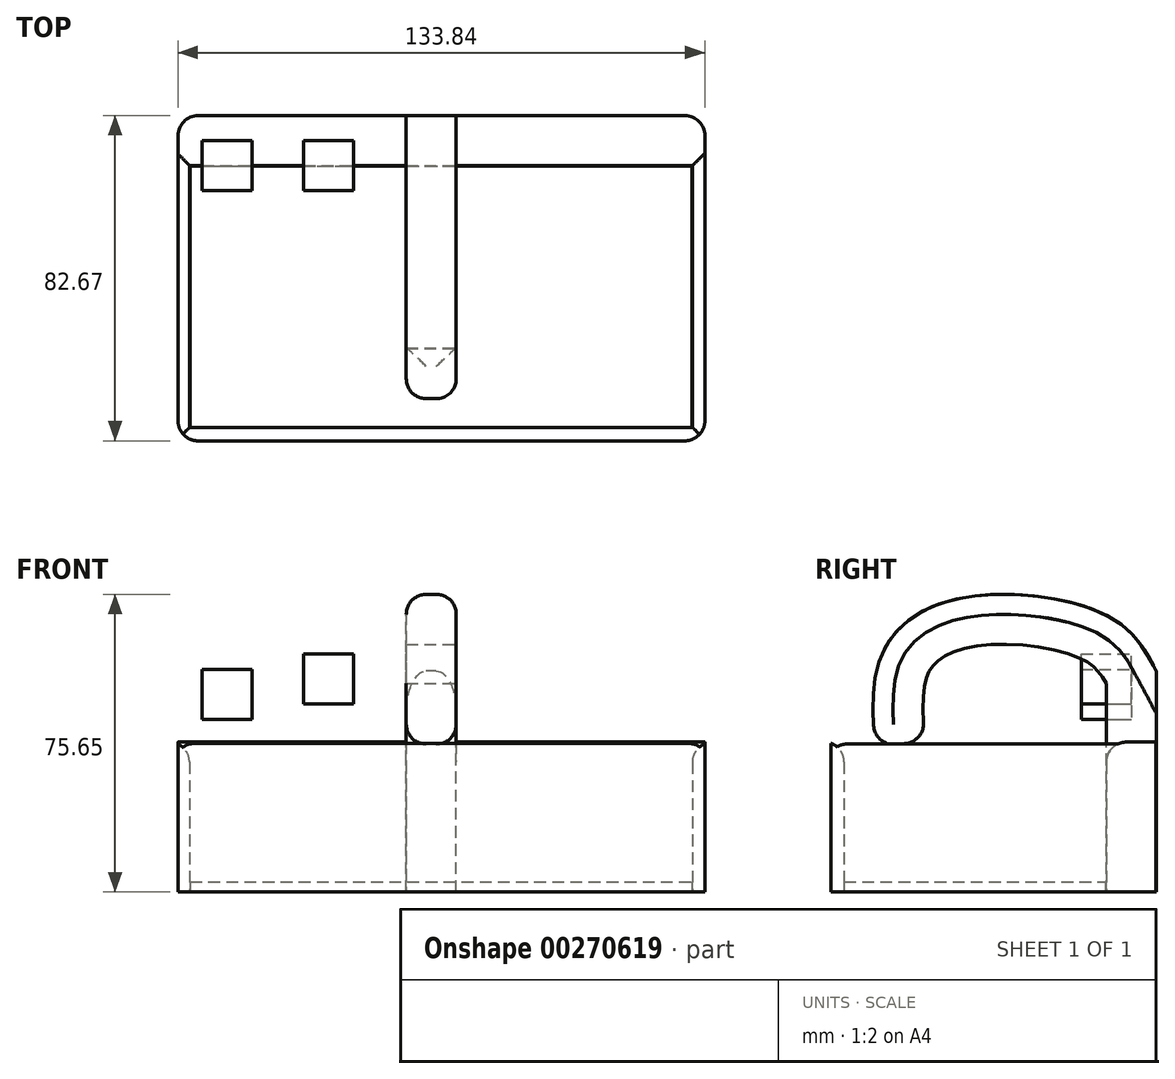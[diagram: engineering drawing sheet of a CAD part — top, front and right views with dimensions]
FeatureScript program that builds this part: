
annotation { "Feature Type Name" : "Feature", "Feature Type Description" : "" }
export const myFeature = defineFeature(function(context is Context, id is Id, definition is map)
    precondition{}
    {
        {
            var Q0;
            Q0=qCreatedBy(makeId("Top.planeOp"),FACE);
            var sketch = newSketch(context, id + "F0", { "sketchPlane" : qUnion([Q0])});
            skLineSegment(sketch, "E0.bottom", {"start": v(-6.35, 6.35) * mm, "end": v(6.35, 6.35) * mm});
            skLineSegment(sketch, "E0.top", {"start": v(-6.35, -6.35) * mm, "end": v(6.35, -6.35) * mm});
            skLineSegment(sketch, "E0.left", {"start": v(-6.35, 6.35) * mm, "end": v(-6.35, -6.35) * mm});
            skLineSegment(sketch, "E0.right", {"start": v(6.35, 6.35) * mm, "end": v(6.35, -6.35) * mm});
            skPoint(sketch, "E0.middle", {"position": v(0, 0) * mm});
            skSolve(sketch);
        }
        {
            var Q0;
            Q0=qCreatedBy(makeId("Right.planeOp"),FACE);
            var sketch = newSketch(context, id + "F1", { "sketchPlane" : qUnion([Q0])});
            skLineSegment(sketch, "E1", {"start": v(0, 0) * mm, "end": v(0, 54.57) * mm});
            skLineSegment(sketch, "E2", {"start": v(0, -0.8) * mm, "end": v(0, -38.9) * mm});
            skFitSpline(sketch, "E3", {"points": [v(0, 54.57) * mm, v(-8.3, 64.16) * mm, v(-40.1, 68.78) * mm, v(-57.07, 58.87) * mm, v(-58.75, 37.62) * mm], "startDerivative": vector(-28.75, 53.69) * mm, "endDerivative": vector(7.18, -92.92) * mm});
            skSolve(sketch);
        }
        {
            var Q0;
            Q0=makeQuery(id+"F0.imprint","IMPRINT",FACE,{"disambiguationData":[TD([[makeQuery(id+"F0.imprint","IMPRINT",EDGE,{"derivedFrom":sQuery(id+"F0.wireOp",EDGE,"E0.bottom")}),-1.0]])]});
            var Q1;
            Q1=sQuery(id+"F1.wireOp",EDGE,"E3");
            var Q2;
            Q2=sQuery(id+"F1.wireOp",EDGE,"E1");
            sweep(context, id + "F2", {"profiles" : qUnion([Q0]), "path" : qUnion([Q1, Q2])});
        }
        {
            var Q0;
            Q0=qCreatedBy(makeId("Top.planeOp"),FACE);
            var sketch = newSketch(context, id + "F3", { "sketchPlane" : qUnion([Q0])});
            skLineSegment(sketch, "E4.bottom", {"start": v(-64.34, 6.27) * mm, "end": v(69.5, 6.27) * mm});
            skLineSegment(sketch, "E4.top", {"start": v(-64.34, -76.32) * mm, "end": v(69.5, -76.32) * mm});
            skLineSegment(sketch, "E4.left", {"start": v(-64.34, 6.27) * mm, "end": v(-64.34, -76.32) * mm});
            skLineSegment(sketch, "E4.right", {"start": v(69.5, 6.27) * mm, "end": v(69.5, -76.32) * mm});
            skLineSegment(sketch, "E5.bottom", {"start": v(-61.44, -6.33) * mm, "end": v(66.42, -6.33) * mm});
            skLineSegment(sketch, "E5.top", {"start": v(-61.44, -72.94) * mm, "end": v(66.42, -72.94) * mm});
            skLineSegment(sketch, "E5.left", {"start": v(-61.44, -6.33) * mm, "end": v(-61.44, -72.94) * mm});
            skLineSegment(sketch, "E5.right", {"start": v(66.42, -6.33) * mm, "end": v(66.42, -72.94) * mm});
            skSolve(sketch);
        }
        {
            var Q0;
            Q0=makeQuery(id+"F3.imprint","IMPRINT",FACE,{"disambiguationData":[TD([[makeQuery(id+"F3.imprint","IMPRINT",EDGE,{"derivedFrom":sQuery(id+"F3.wireOp",EDGE,"E4.bottom")}),-1.0]])]});
            extrude(context, id + "F4", {"entities" : qUnion([Q0]), "operationType" : NewBodyOperationType.ADD, "depth" : 38.1 * mm});
        }
        {
            var Q0;
            Q0=qCreatedBy(makeId("Top.planeOp"),FACE);
            var sketch = newSketch(context, id + "F5", { "sketchPlane" : qUnion([Q0])});
            skLineSegment(sketch, "E6.bottom", {"start": v(-61.26, -72.94) * mm, "end": v(66.24, -72.94) * mm});
            skLineSegment(sketch, "E6.top", {"start": v(-61.26, -6.52) * mm, "end": v(66.24, -6.52) * mm});
            skLineSegment(sketch, "E6.left", {"start": v(-61.26, -72.94) * mm, "end": v(-61.26, -6.52) * mm});
            skLineSegment(sketch, "E6.right", {"start": v(66.24, -72.94) * mm, "end": v(66.24, -6.52) * mm});
            skSolve(sketch);
        }
        {
            var Q0;
            Q0=makeQuery(id+"F5.imprint","IMPRINT",FACE,{"disambiguationData":[TD([[makeQuery(id+"F5.imprint","IMPRINT",EDGE,{"derivedFrom":sQuery(id+"F5.wireOp",EDGE,"E6.bottom")}),1.0]])]});
            extrude(context, id + "F6", {"entities" : qUnion([Q0]), "operationType" : NewBodyOperationType.ADD, "depth" : 2.54 * mm});
        }
        {
            var Q0;
            {var subQ0=sQuery(id+"F3.wireOp",EDGE,"E5.left");var subQ1=sQuery(id+"F3.wireOp",EDGE,"E5.bottom");Q0=makeQuery(id+"F4.boolean.opBoolean","SPLIT",EDGE,{"disambiguationData":[TD([makeQuery(id+"F4.opExtrude","SWEPT_FACE",FACE,{"disambiguationData":[OSD([subQ0])]})])],"derivedFrom":makeQuery(id+"F4.opExtrude","CAP_EDGE",EDGE,{"disambiguationData":[OSD([subQ1])],"isStart":false})});}
            var Q1;
            Q1=makeQuery(id+"F4.opExtrude","CAP_EDGE",EDGE,{"disambiguationData":[OSD([sQuery(id+"F3.wireOp",EDGE,"E5.left")])],"isStart":false});
            var Q2;
            Q2=makeQuery(id+"F4.opExtrude","CAP_EDGE",EDGE,{"disambiguationData":[OSD([sQuery(id+"F3.wireOp",EDGE,"E5.top")])],"isStart":false});
            var Q3;
            Q3=makeQuery(id+"F4.opExtrude","CAP_EDGE",EDGE,{"disambiguationData":[OSD([sQuery(id+"F3.wireOp",EDGE,"E5.right")])],"isStart":false});
            var Q4;
            {var subQ0=sQuery(id+"F3.wireOp",EDGE,"E5.right");var subQ1=sQuery(id+"F3.wireOp",EDGE,"E5.bottom");Q4=makeQuery(id+"F4.boolean.opBoolean","SPLIT",EDGE,{"disambiguationData":[TD([makeQuery(id+"F4.opExtrude","SWEPT_FACE",FACE,{"disambiguationData":[OSD([subQ0])]})])],"derivedFrom":makeQuery(id+"F4.opExtrude","CAP_EDGE",EDGE,{"disambiguationData":[OSD([subQ1])],"isStart":false})});}
            var Q5;
            Q5=makeQuery(id+"F2.opSweep","SWEPT_EDGE",EDGE,{"disambiguationData":[OSD([sQuery(id+"F0.wireOp",EDGE,"E0.bottom"),sQuery(id+"F0.wireOp",EDGE,"E0.right"),sQuery(id+"F1.wireOp",EDGE,"E3")]),OD(0.0)]});
            var Q6;
            Q6=makeQuery(id+"F2.opSweep","SWEPT_EDGE",EDGE,{"disambiguationData":[OSD([sQuery(id+"F0.wireOp",EDGE,"E0.bottom"),sQuery(id+"F0.wireOp",EDGE,"E0.left"),sQuery(id+"F1.wireOp",EDGE,"E3")]),OD(0.0)]});
            var Q7;
            Q7=makeQuery(id+"F2.opSweep","CAP_EDGE",EDGE,{"disambiguationData":[OSD([sQuery(id+"F0.wireOp",EDGE,"E0.bottom"),sQuery(id+"F1.wireOp",VERTEX,"E3.end")])],"isStart":false});
            var Q8;
            Q8=makeQuery(id+"F2.opSweep","CAP_EDGE",EDGE,{"disambiguationData":[OSD([sQuery(id+"F0.wireOp",EDGE,"E0.right"),sQuery(id+"F1.wireOp",VERTEX,"E3.end")])],"isStart":false});
            var Q9;
            Q9=makeQuery(id+"F2.opSweep","CAP_EDGE",EDGE,{"disambiguationData":[OSD([sQuery(id+"F0.wireOp",EDGE,"E0.top"),sQuery(id+"F1.wireOp",VERTEX,"E3.end")])],"isStart":false});
            var Q10;
            Q10=makeQuery(id+"F2.opSweep","CAP_EDGE",EDGE,{"disambiguationData":[OSD([sQuery(id+"F0.wireOp",EDGE,"E0.left"),sQuery(id+"F1.wireOp",VERTEX,"E3.end")])],"isStart":false});
            var Q11;
            Q11=makeQuery(id+"F4.opExtrude","SWEPT_EDGE",EDGE,{"disambiguationData":[OSD([sQuery(id+"F3.wireOp",EDGE,"E4.top"),sQuery(id+"F3.wireOp",EDGE,"E4.left")])]});
            var Q12;
            Q12=makeQuery(id+"F4.opExtrude","SWEPT_EDGE",EDGE,{"disambiguationData":[OSD([sQuery(id+"F3.wireOp",EDGE,"E4.bottom"),sQuery(id+"F3.wireOp",EDGE,"E4.left")])]});
            var Q13;
            Q13=makeQuery(id+"F4.opExtrude","SWEPT_EDGE",EDGE,{"disambiguationData":[OSD([sQuery(id+"F3.wireOp",EDGE,"E4.bottom"),sQuery(id+"F3.wireOp",EDGE,"E4.right")])]});
            var Q14;
            Q14=makeQuery(id+"F4.opExtrude","SWEPT_EDGE",EDGE,{"disambiguationData":[OSD([sQuery(id+"F3.wireOp",EDGE,"E4.top"),sQuery(id+"F3.wireOp",EDGE,"E4.right")])]});
            fillet(context, id + "F7", {"entities" : qUnion([Q0, Q1, Q2, Q3, Q4, Q5, Q6, Q7, Q8, Q9, Q10, Q11, Q12, Q13, Q14]), "radius" : 5.08 * mm, "tangentPropagation" : true, "allowEdgeOverflow" : false});
        }
        {
            var Q0;
            Q0=qCreatedBy(makeId("Front.planeOp"),FACE);
            var sketch = newSketch(context, id + "F8", { "sketchPlane" : qUnion([Q0])});
            skLineSegment(sketch, "E7.bottom", {"start": v(-32.45, 47.75) * mm, "end": v(-19.75, 47.75) * mm});
            skLineSegment(sketch, "E7.top", {"start": v(-32.45, 60.45) * mm, "end": v(-19.75, 60.45) * mm});
            skLineSegment(sketch, "E7.left", {"start": v(-32.45, 47.75) * mm, "end": v(-32.45, 60.45) * mm});
            skLineSegment(sketch, "E7.right", {"start": v(-19.75, 47.75) * mm, "end": v(-19.75, 60.45) * mm});
            skLineSegment(sketch, "E8.bottom", {"start": v(-58.24, 56.58) * mm, "end": v(-45.54, 56.58) * mm});
            skLineSegment(sketch, "E8.top", {"start": v(-58.24, 43.88) * mm, "end": v(-45.54, 43.88) * mm});
            skLineSegment(sketch, "E8.left", {"start": v(-58.24, 56.58) * mm, "end": v(-58.24, 43.88) * mm});
            skLineSegment(sketch, "E8.right", {"start": v(-45.54, 56.58) * mm, "end": v(-45.54, 43.88) * mm});
            skSolve(sketch);
        }
        {
            var Q0;
            Q0 = qSketchRegion(id + "F8", true);
            extrude(context, id + "F9", {"entities" : qUnion([Q0]), "depth" : 12.7 * mm});
        }
    });
